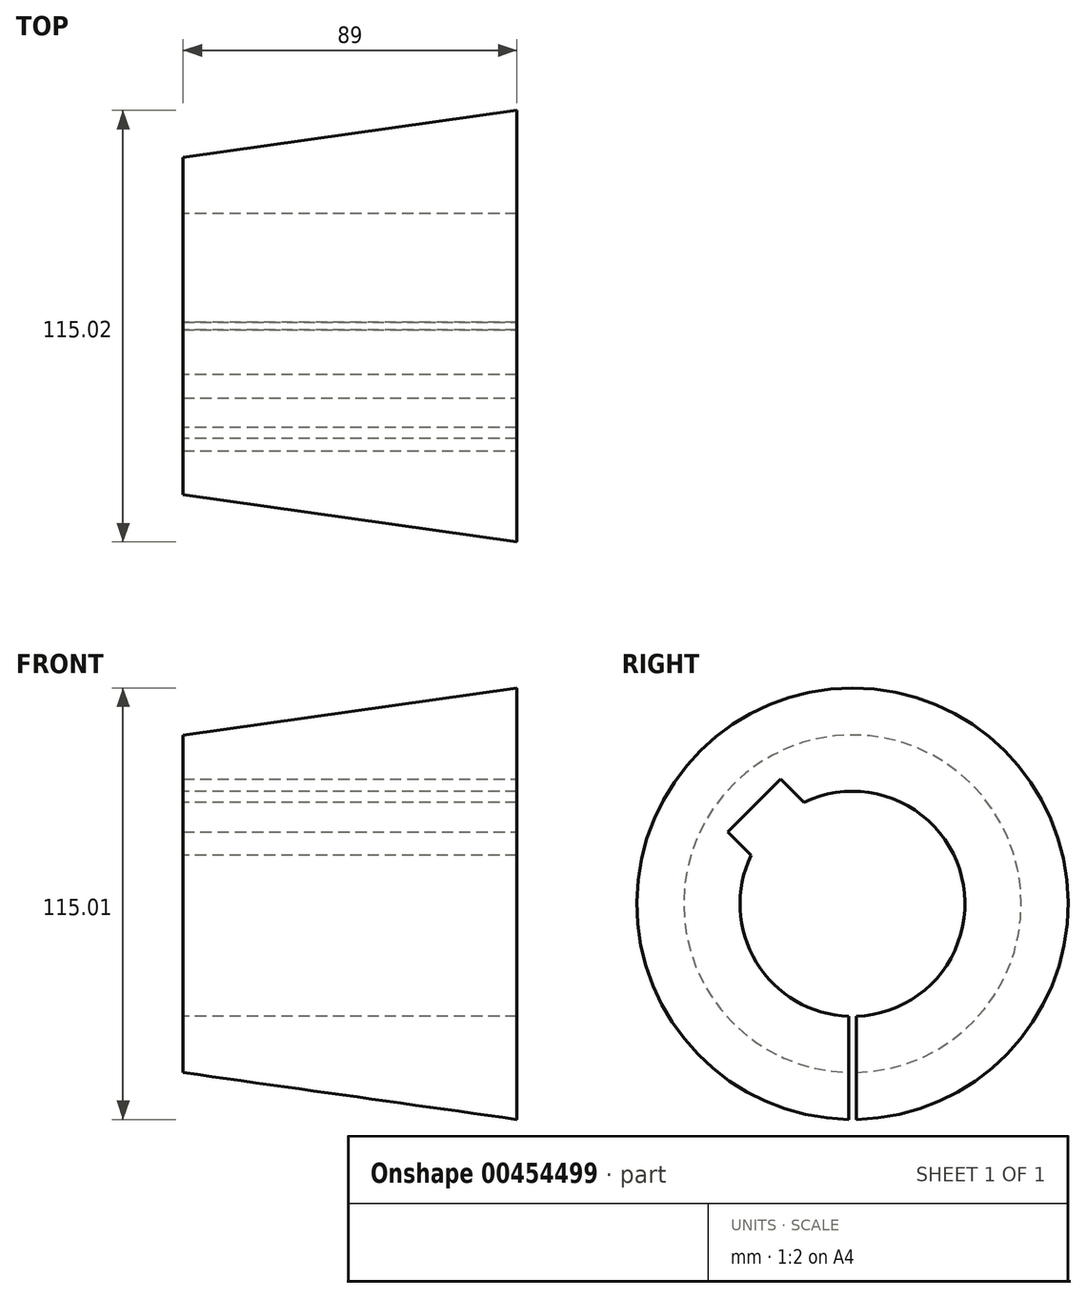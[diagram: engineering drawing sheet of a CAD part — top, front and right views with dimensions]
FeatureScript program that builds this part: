
annotation { "Feature Type Name" : "Feature", "Feature Type Description" : "" }
export const myFeature = defineFeature(function(context is Context, id is Id, definition is map)
    precondition{}
    {
        {
            var Q0;
            Q0=qCreatedBy(makeId("Front.planeOp"),FACE);
            var sketch = newSketch(context, id + "F0", { "sketchPlane" : qUnion([Q0])});
            skLineSegment(sketch, "E0", {"start": v(-44.5, 30) * mm, "end": v(44.5, 30) * mm});
            skLineSegment(sketch, "E1", {"start": v(44.5, 30) * mm, "end": v(44.5, 57.5) * mm});
            skLineSegment(sketch, "E2", {"start": v(44.5, 57.5) * mm, "end": v(-44.5, 45) * mm});
            skLineSegment(sketch, "E3", {"start": v(-44.5, 45) * mm, "end": v(-44.5, 30) * mm});
            skLineSegment(sketch, "E4", {"start": v(-51.4, 0) * mm, "end": v(60, 0) * mm, "construction": true});
            skSolve(sketch);
        }
        {
            var Q0;
            Q0 = qSketchRegion(id + "F0", true);
            var Q1;
            Q1=sQuery(id+"F0.wireOp",EDGE,"E4");
            revolve(context, id + "F1", {"entities" : qUnion([Q0]), "axis" : qUnion([Q1]), "revolveType" : RevolveType.FULL});
        }
        {
            var Q0;
            Q0=makeQuery(id+"F1.opRevolve","SWEPT_FACE",FACE,{"disambiguationData":[OSD([sQuery(id+"F0.wireOp",EDGE,"E1")])]});
            var sketch = newSketch(context, id + "F2", { "sketchPlane" : qUnion([Q0])});
            skLineSegment(sketch, "E5.bottom", {"start": v(-1, -29.22) * mm, "end": v(1, -29.22) * mm});
            skLineSegment(sketch, "E5.top", {"start": v(-1, -64.72) * mm, "end": v(1, -64.72) * mm});
            skLineSegment(sketch, "E5.left", {"start": v(-1, -29.22) * mm, "end": v(-1, -64.72) * mm});
            skLineSegment(sketch, "E5.right", {"start": v(1, -29.22) * mm, "end": v(1, -64.72) * mm});
            skSolve(sketch);
        }
        {
            var Q0;
            Q0 = qSketchRegion(id + "F2", true);
            extrude(context, id + "F3", {"entities" : qUnion([Q0]), "operationType" : NewBodyOperationType.REMOVE, "endBound" : BoundingType.THROUGH_ALL, "oppositeDirection" : true, "depth" : 25 * mm});
        }
        {
            var Q0;
            Q0=makeQuery(id+"F1.opRevolve","SWEPT_FACE",FACE,{"disambiguationData":[OSD([sQuery(id+"F0.wireOp",EDGE,"E1")])]});
            var sketch = newSketch(context, id + "F4", { "sketchPlane" : qUnion([Q0])});
            skCircle(sketch, "E6", {"center": v(-60, 0) * mm, "radius": 9.38 * mm});
            skCircle(sketch, "E7", {"center": v(0, 0) * mm, "radius": 60 * mm, "construction": true});
            skSolve(sketch);
        }
        {
            var Q0;
            Q0=makeQuery(id+"F1.opRevolve","SWEPT_FACE",FACE,{"disambiguationData":[OSD([sQuery(id+"F0.wireOp",EDGE,"E1")])]});
            var sketch = newSketch(context, id + "F5", { "sketchPlane" : qUnion([Q0])});
            skLineSegment(sketch, "E8", {"start": v(0, 0) * mm, "end": v(-67.04, 67.04) * mm, "construction": true});
            skLineSegment(sketch, "E9.0", {"start": v(-19.16, 33.3) * mm, "end": v(-9.38, 23.52) * mm});
            skLineSegment(sketch, "E9.1", {"start": v(-9.38, 23.52) * mm, "end": v(-23.52, 9.38) * mm});
            skLineSegment(sketch, "E9.2", {"start": v(-23.52, 9.38) * mm, "end": v(-33.3, 19.16) * mm});
            skLineSegment(sketch, "E9.3", {"start": v(-33.3, 19.16) * mm, "end": v(-19.16, 33.3) * mm});
            skPoint(sketch, "E9.0.midPoint", {"position": v(-14.27, 28.41) * mm});
            skSolve(sketch);
        }
        {
            var Q0;
            Q0 = qSketchRegion(id + "F5", true);
            extrude(context, id + "F6", {"entities" : qUnion([Q0]), "operationType" : NewBodyOperationType.REMOVE, "endBound" : BoundingType.THROUGH_ALL, "oppositeDirection" : true, "depth" : 25 * mm});
        }
    });
